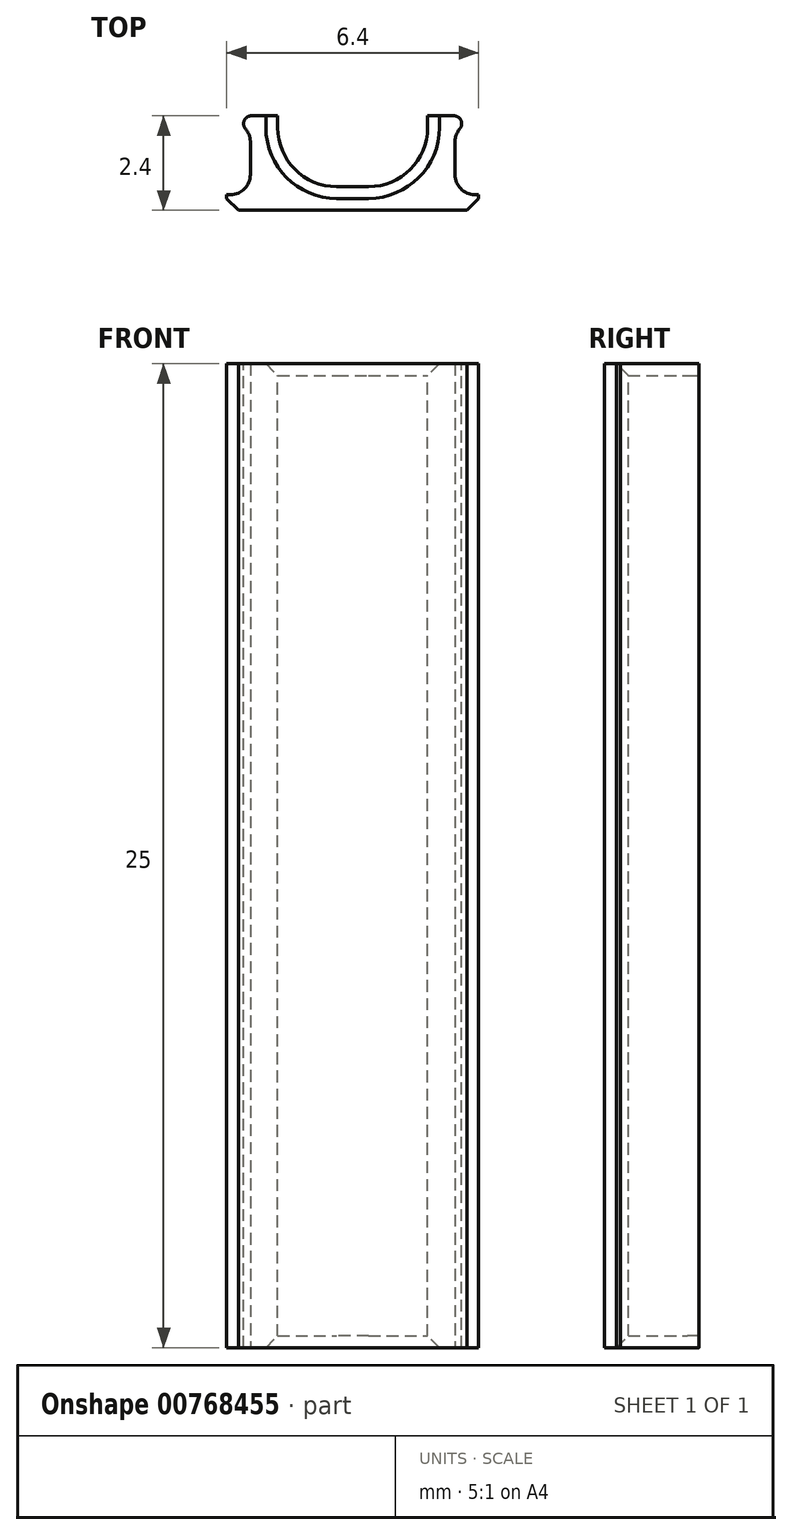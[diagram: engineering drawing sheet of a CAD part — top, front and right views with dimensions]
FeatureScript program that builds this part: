
annotation { "Feature Type Name" : "Feature", "Feature Type Description" : "" }
export const myFeature = defineFeature(function(context is Context, id is Id, definition is map)
    precondition{}
    {
        {
            var Q0;
            Q0=qCreatedBy(makeId("Top.planeOp"),FACE);
            var sketch = newSketch(context, id + "F0", { "sketchPlane" : qUnion([Q0])});
            skLineSegment(sketch, "E0", {"start": v(0, 0) * mm, "end": v(0, 0.4) * mm});
            skLineSegment(sketch, "E1", {"start": v(0, 0.4) * mm, "end": v(0.6, 0.4) * mm});
            skLineSegment(sketch, "E2", {"start": v(0.6, 0.4) * mm, "end": v(0.6, 2.2) * mm});
            skLineSegment(sketch, "E3", {"start": v(0.6, 2.2) * mm, "end": v(0.3, 2.2) * mm});
            skLineSegment(sketch, "E4", {"start": v(0.3, 2.2) * mm, "end": v(0.3, 2.4) * mm});
            skLineSegment(sketch, "E5", {"start": v(0.3, 2.4) * mm, "end": v(6.1, 2.4) * mm});
            skLineSegment(sketch, "E6", {"start": v(6.1, 2.4) * mm, "end": v(6.1, 2.2) * mm});
            skLineSegment(sketch, "E7", {"start": v(6.1, 2.2) * mm, "end": v(5.8, 2.2) * mm});
            skLineSegment(sketch, "E8", {"start": v(5.8, 2.2) * mm, "end": v(5.8, 0.4) * mm});
            skLineSegment(sketch, "E9", {"start": v(5.8, 0.4) * mm, "end": v(6.4, 0.4) * mm});
            skLineSegment(sketch, "E10", {"start": v(6.4, 0.4) * mm, "end": v(6.4, 0) * mm});
            skLineSegment(sketch, "E11", {"start": v(6.4, 0) * mm, "end": v(0, 0) * mm});
            skSolve(sketch);
        }
        {
            var Q0;
            Q0=makeQuery(id+"F0.imprint","IMPRINT",FACE,{"disambiguationData":[TD([[makeQuery(id+"F0.imprint","IMPRINT",EDGE,{"derivedFrom":sQuery(id+"F0.wireOp",EDGE,"E0")}),-1.0]])]});
            extrude(context, id + "F1", {"entities" : qUnion([Q0]), "depth" : 25 * mm, "offsetDistance" : 25 * mm});
        }
        {
            var Q0;
            Q0=makeQuery(id+"F1.opExtrude","SWEPT_EDGE",EDGE,{"disambiguationData":[OSD([sQuery(id+"F0.wireOp",EDGE,"E2"),sQuery(id+"F0.wireOp",EDGE,"E3")])]});
            var Q1;
            Q1=makeQuery(id+"F1.opExtrude","SWEPT_EDGE",EDGE,{"disambiguationData":[OSD([sQuery(id+"F0.wireOp",EDGE,"E7"),sQuery(id+"F0.wireOp",EDGE,"E8")])]});
            fillet(context, id + "F2", {"entities" : qUnion([Q0, Q1]), "radius" : 0.5 * mm, "tangentPropagation" : true, "allowEdgeOverflow" : false});
        }
        {
            var Q0;
            Q0=makeQuery(id+"F1.opExtrude","SWEPT_EDGE",EDGE,{"disambiguationData":[OSD([sQuery(id+"F0.wireOp",EDGE,"E8"),sQuery(id+"F0.wireOp",EDGE,"E9")])]});
            var Q1;
            Q1=makeQuery(id+"F1.opExtrude","SWEPT_EDGE",EDGE,{"disambiguationData":[OSD([sQuery(id+"F0.wireOp",EDGE,"E1"),sQuery(id+"F0.wireOp",EDGE,"E2")])]});
            fillet(context, id + "F3", {"entities" : qUnion([Q0, Q1]), "radius" : 0.5 * mm, "tangentPropagation" : true, "allowEdgeOverflow" : false});
        }
        {
            var Q0;
            Q0=makeQuery(id+"F1.opExtrude","SWEPT_EDGE",EDGE,{"disambiguationData":[OSD([sQuery(id+"F0.wireOp",EDGE,"E4"),sQuery(id+"F0.wireOp",EDGE,"E5")])]});
            var Q1;
            Q1=makeQuery(id+"F1.opExtrude","SWEPT_EDGE",EDGE,{"disambiguationData":[OSD([sQuery(id+"F0.wireOp",EDGE,"E5"),sQuery(id+"F0.wireOp",EDGE,"E6")])]});
            fillet(context, id + "F4", {"entities" : qUnion([Q0, Q1]), "radius" : 0.4 * mm, "tangentPropagation" : true, "allowEdgeOverflow" : false});
        }
        {
            var Q0;
            Q0=makeQuery(id+"F4.opFillet","BLEND_EDGE",EDGE,{"blendedFrom":[makeQuery(id+"F1.opExtrude","SWEPT_EDGE",EDGE,{"disambiguationData":[OSD([sQuery(id+"F0.wireOp",EDGE,"E4"),sQuery(id+"F0.wireOp",EDGE,"E5")])]}),makeQuery(id+"F2.opFillet","BLEND_FACE",FACE,{"disambiguationData":[OSD([sQuery(id+"F0.wireOp",EDGE,"E2"),sQuery(id+"F0.wireOp",EDGE,"E3")])]})],"blendedInto":[makeQuery(id+"F2.opFillet","BLEND_FACE",FACE,{"disambiguationData":[OSD([sQuery(id+"F0.wireOp",EDGE,"E2"),sQuery(id+"F0.wireOp",EDGE,"E3")])]})]});
            var Q1;
            Q1=makeQuery(id+"F4.opFillet","BLEND_EDGE",EDGE,{"blendedFrom":[makeQuery(id+"F1.opExtrude","SWEPT_EDGE",EDGE,{"disambiguationData":[OSD([sQuery(id+"F0.wireOp",EDGE,"E5"),sQuery(id+"F0.wireOp",EDGE,"E6")])]}),makeQuery(id+"F2.opFillet","BLEND_FACE",FACE,{"disambiguationData":[OSD([sQuery(id+"F0.wireOp",EDGE,"E7"),sQuery(id+"F0.wireOp",EDGE,"E8")])]})],"blendedInto":[makeQuery(id+"F2.opFillet","BLEND_FACE",FACE,{"disambiguationData":[OSD([sQuery(id+"F0.wireOp",EDGE,"E7"),sQuery(id+"F0.wireOp",EDGE,"E8")])]})]});
            fillet(context, id + "F5", {"entities" : qUnion([Q0, Q1]), "radius" : 0.2 * mm, "tangentPropagation" : true, "allowEdgeOverflow" : false});
        }
        {
            var Q0;
            Q0=makeQuery(id+"F1.opExtrude","CAP_FACE",FACE,{"disambiguationData":[OSD([sQuery(id+"F0.wireOp",EDGE,"E0"),sQuery(id+"F0.wireOp",EDGE,"E1"),sQuery(id+"F0.wireOp",EDGE,"E2"),sQuery(id+"F0.wireOp",EDGE,"E3"),sQuery(id+"F0.wireOp",EDGE,"E4"),sQuery(id+"F0.wireOp",EDGE,"E5"),sQuery(id+"F0.wireOp",EDGE,"E6"),sQuery(id+"F0.wireOp",EDGE,"E7"),sQuery(id+"F0.wireOp",EDGE,"E8"),sQuery(id+"F0.wireOp",EDGE,"E9"),sQuery(id+"F0.wireOp",EDGE,"E10"),sQuery(id+"F0.wireOp",EDGE,"E11")])],"isStart":false});
            var sketch = newSketch(context, id + "F6", { "sketchPlane" : qUnion([Q0])});
            skLineSegment(sketch, "E12.bottom", {"start": v(5.1, 2.4) * mm, "end": v(1.3, 2.4) * mm});
            skLineSegment(sketch, "E12.top", {"start": v(5.1, 0.6) * mm, "end": v(1.3, 0.6) * mm});
            skLineSegment(sketch, "E12.left", {"start": v(5.1, 2.4) * mm, "end": v(5.1, 0.6) * mm});
            skLineSegment(sketch, "E12.right", {"start": v(1.3, 2.4) * mm, "end": v(1.3, 0.6) * mm});
            skPoint(sketch, "E12.middle", {"position": v(3.2, 1.5) * mm});
            skPoint(sketch, "E12.middle.positionSnap0", {"position": v(3.2, 2.4) * mm});
            skPoint(sketch, "E12.centerSnap0", {"position": v(3.2, 2.4) * mm});
            skSolve(sketch);
        }
        {
            var Q0;
            Q0 = qSketchRegion(id + "F6", true);
            extrude(context, id + "F7", {"entities" : qUnion([Q0]), "operationType" : NewBodyOperationType.REMOVE, "endBound" : BoundingType.THROUGH_ALL, "oppositeDirection" : true, "depth" : 25 * mm, "offsetDistance" : 25 * mm});
        }
        {
            var Q0;
            Q0=makeQuery(id+"F7.boolean.opBoolean","COPY",EDGE,{"derivedFrom":makeQuery(id+"F7.opExtrude","SWEPT_EDGE",EDGE,{"disambiguationData":[OSD([sQuery(id+"F6.wireOp",EDGE,"E12.top"),sQuery(id+"F6.wireOp",EDGE,"E12.right")])]})});
            var Q1;
            Q1=makeQuery(id+"F7.boolean.opBoolean","COPY",EDGE,{"derivedFrom":makeQuery(id+"F7.opExtrude","SWEPT_EDGE",EDGE,{"disambiguationData":[OSD([sQuery(id+"F6.wireOp",EDGE,"E12.top"),sQuery(id+"F6.wireOp",EDGE,"E12.left")])]})});
            fillet(context, id + "F8", {"entities" : qUnion([Q0, Q1]), "radius" : 1.5 * mm, "tangentPropagation" : true, "allowEdgeOverflow" : false});
        }
        {
            var Q0;
            Q0=makeQuery(id+"F7.boolean.opBoolean","COPY",FACE,{"derivedFrom":makeQuery(id+"F7.opExtrude","SWEPT_FACE",FACE,{"disambiguationData":[OSD([sQuery(id+"F6.wireOp",EDGE,"E12.top")])]})});
            var Q1;
            Q1=makeQuery(id+"F1.opExtrude","SWEPT_EDGE",EDGE,{"disambiguationData":[OSD([sQuery(id+"F0.wireOp",EDGE,"E10"),sQuery(id+"F0.wireOp",EDGE,"E11")])]});
            var Q2;
            Q2=makeQuery(id+"F1.opExtrude","SWEPT_EDGE",EDGE,{"disambiguationData":[OSD([sQuery(id+"F0.wireOp",EDGE,"E0"),sQuery(id+"F0.wireOp",EDGE,"E11")])]});
            chamfer(context, id + "F9", {"entities" : qUnion([Q0, Q1, Q2]), "width" : 0.3 * mm, "tangentPropagation" : true});
        }
    });
